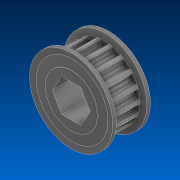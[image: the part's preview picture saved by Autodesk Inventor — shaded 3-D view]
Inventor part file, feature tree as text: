
AUTODESK INVENTOR PART (.ipt)
format: ipt  version: 2022.2 (Build 262287000, 287)  size: 501,248 bytes
history: native  units: in
note: dims shown in document units (in); Inventor stores cm internally (conversion verified against a paired STEP export)
features: mirror x1
ambient origin geometry x8: Origin, YZ Plane, XZ Plane, XY Plane, X Axis, Y Axis, Z Axis, Center Point
bodies: Solid1 (feature_tree)
feature tree (1):
  mirror  "Mirror1"
